# Revit family: 63_UN_LF_Surface-Mounted-Titan-Angle-45-13_LI
name_source: partatom
category: Lighting Fixtures
units: mm (PartAtom-declared; Revit-internal decimal feet)

## family parameters
Always vertical = Yes
Cut with Voids When Loaded = Yes
Light Source = No
OmniClass Number = 23.80.70.11.14.11
OmniClass Title = Downlights
Part Type = Normal
Room Calculation Point = Yes
Round Connector Dimension = Use Diameter
Shared = No
Work Plane-Based = No

## types (3) — shared parameters
Assembly Code = 63.0
Housing_Material = Plastic, Opaque Black
IfcExportAs = IfcLightFixtureType
IfcExportType = USERDEFINED
Lamp = LED
Manufacturer = Light International
Model = TITAN Angle 45
URL = https://lightinternational.nl
Voltage = 230 V

## per-type parameters (varying)
| type | Apparent Load | Light Source | Luminous Flux (lm) | Type Comments | Wattage Comments |
| TA45133 - Wall mounted | 18 VA | TA4513 Geometry : TA45133 Geometry | 3212 lm | TA45133 | 18.4W |
| TA45134 - Wall mounted | 23 VA | TA4513 Geometry : TA45134 Geometry | 4228 lm | TA45134 | 23.4W |
| TA45135 - Wall mounted | 38 VA | TA4513 Geometry : TA45135 Geometry | 6473 lm | TA45135 | 37.9W |

## geometry (parser evidence)
native form markers: Sweep x19
no freeform markers — native parametric forms only
